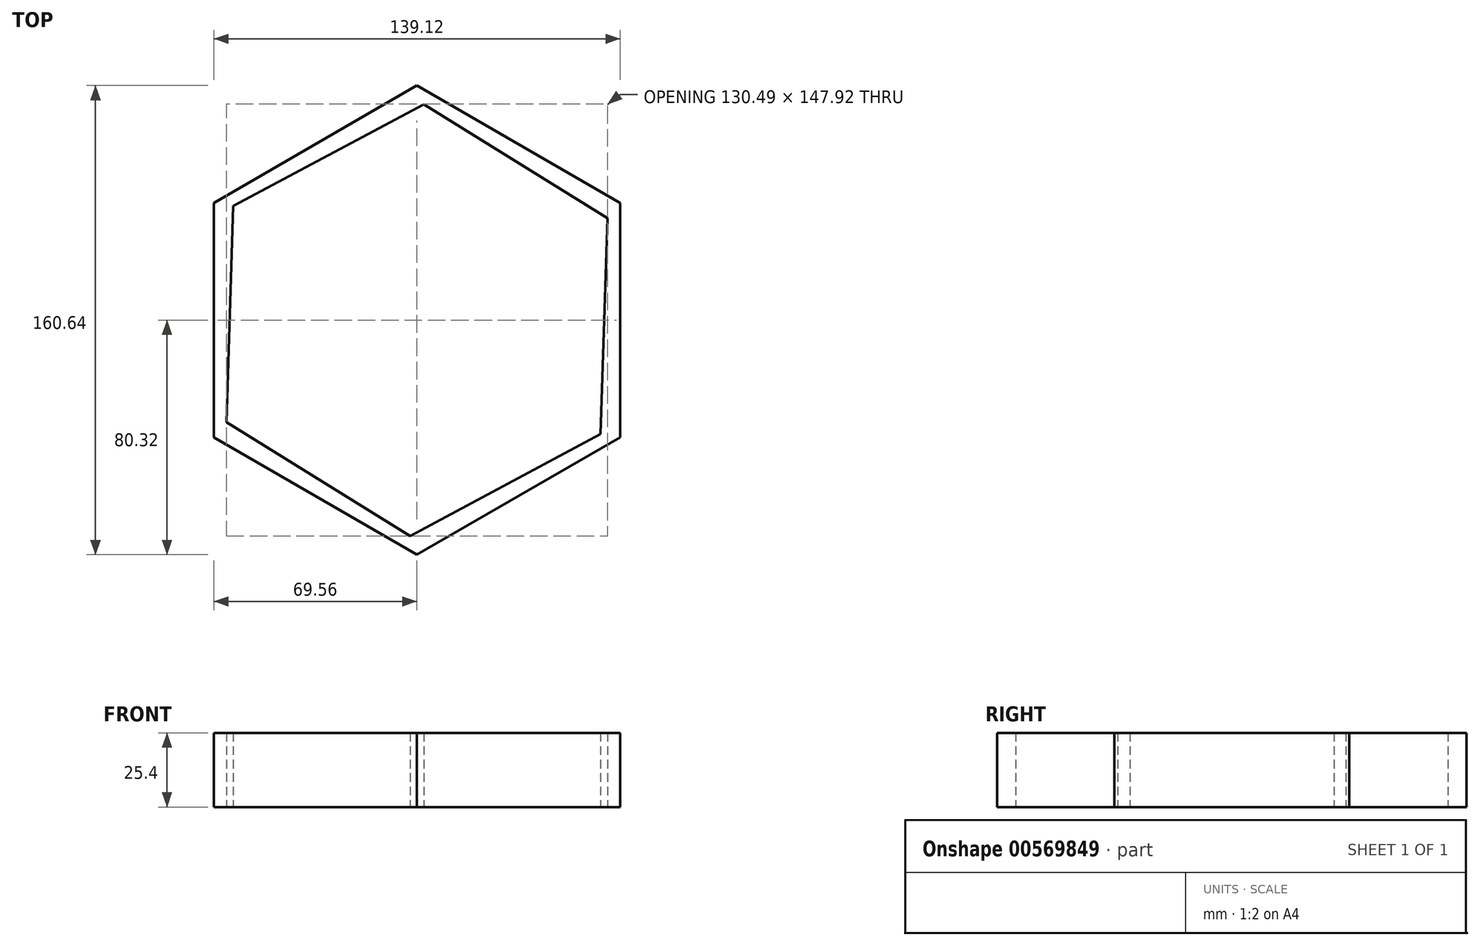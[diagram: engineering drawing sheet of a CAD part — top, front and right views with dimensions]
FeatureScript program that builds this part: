
annotation { "Feature Type Name" : "Feature", "Feature Type Description" : "" }
export const myFeature = defineFeature(function(context is Context, id is Id, definition is map)
    precondition{}
    {
        {
            var Q0;
            Q0=qCreatedBy(makeId("Top.planeOp"),FACE);
            var sketch = newSketch(context, id + "F0", { "sketchPlane" : qUnion([Q0])});
            skCircle(sketch, "E0.cCircle", {"center": v(0, 0) * mm, "radius": 69.56 * mm, "construction": true});
            skLineSegment(sketch, "E0.0", {"start": v(-69.56, -40.16) * mm, "end": v(-69.56, 40.16) * mm});
            skLineSegment(sketch, "E0.1", {"start": v(-69.56, 40.16) * mm, "end": v(0, 80.32) * mm});
            skLineSegment(sketch, "E0.2", {"start": v(0, 80.32) * mm, "end": v(69.56, 40.16) * mm});
            skLineSegment(sketch, "E0.3", {"start": v(69.56, 40.16) * mm, "end": v(69.56, -40.16) * mm});
            skLineSegment(sketch, "E0.4", {"start": v(69.56, -40.16) * mm, "end": v(0, -80.32) * mm});
            skLineSegment(sketch, "E0.5", {"start": v(0, -80.32) * mm, "end": v(-69.56, -40.16) * mm});
            skPoint(sketch, "E0.0.midPoint", {"position": v(-69.56, 0) * mm});
            skCircle(sketch, "E1.cCircle", {"center": v(0, 0) * mm, "radius": 64.08 * mm, "construction": true});
            skLineSegment(sketch, "E1.0", {"start": v(-62.86, 39.05) * mm, "end": v(2.39, 73.96) * mm});
            skLineSegment(sketch, "E1.1", {"start": v(2.39, 73.96) * mm, "end": v(65.24, 34.91) * mm});
            skLineSegment(sketch, "E1.2", {"start": v(65.24, 34.91) * mm, "end": v(62.86, -39.05) * mm});
            skLineSegment(sketch, "E1.3", {"start": v(62.86, -39.05) * mm, "end": v(-2.39, -73.96) * mm});
            skLineSegment(sketch, "E1.4", {"start": v(-2.39, -73.96) * mm, "end": v(-65.24, -34.91) * mm});
            skLineSegment(sketch, "E1.5", {"start": v(-65.24, -34.91) * mm, "end": v(-62.86, 39.05) * mm});
            skPoint(sketch, "E1.0.midPoint", {"position": v(-30.24, 56.5) * mm});
            skSolve(sketch);
        }
        {
            var Q0;
            Q0 = qSketchRegion(id + "F0", true);
            extrude(context, id + "F1", {"entities" : qUnion([Q0]), "depth" : 25.4 * mm, "offsetDistance" : 25.4 * mm});
        }
    });
